# Revit family: FU_Stool_Sandler_Inga 4-4
name_source: partatom
category: Furniture
units: mm (PartAtom-declared; Revit-internal decimal feet)

## family parameters
Always vertical = Yes
Cut with Voids When Loaded = No
OmniClass Number = 23.40.20.00
OmniClass Title = General Furniture and Specialties
Room Calculation Point = No
Shared = No
Work Plane-Based = No

## types (1)
- Inga 4.4
    Default Elevation = 0 mm  [stored 0 ft]
    Depth = 515 mm  [stored 1.68963 ft]
    Description = Counter Stool with an upholstered back and wooden seat on a solid beech frame.
Produced to custom height per customer specification, from 23.5”-29” seat height
    Height = 1065 mm  [stored 3.49409 ft]
    Manufacturer = Sandler
    Model = Inga 4.4
    URL = https://www.sandlerseating.com
    Width = 470 mm  [stored 1.54199 ft]

note: [stored X ft] marks values corroborated as IEEE doubles in the binary element streams (Revit-internal decimal feet)

## geometry (parser evidence)
native form markers: Sweep x4
no freeform markers — native parametric forms only
